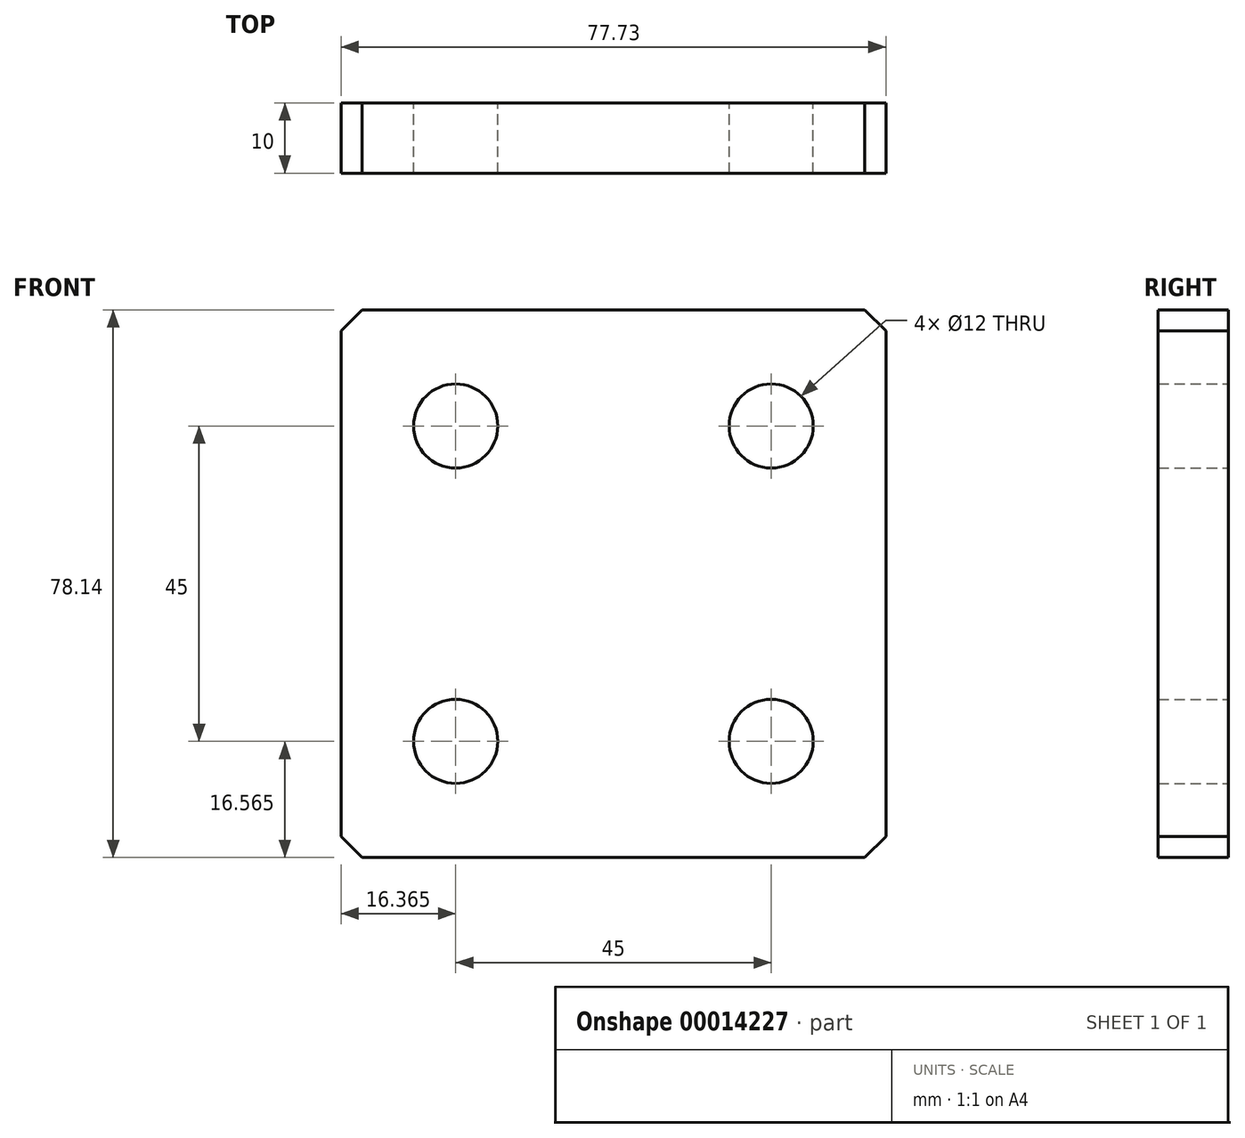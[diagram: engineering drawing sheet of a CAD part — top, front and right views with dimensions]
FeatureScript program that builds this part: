
annotation { "Feature Type Name" : "Feature", "Feature Type Description" : "" }
export const myFeature = defineFeature(function(context is Context, id is Id, definition is map)
    precondition{}
    {
        {
            var Q0;
            Q0=qCreatedBy(makeId("Front.planeOp"),FACE);
            var sketch = newSketch(context, id + "F0", { "sketchPlane" : qUnion([Q0])});
            skPoint(sketch, "E0.rect.middle", {"position": v(-49.6, 29.74) * mm});
            skCircle(sketch, "E1", {"center": v(-27.1, 52.24) * mm, "radius": 6 * mm});
            skCircle(sketch, "E2", {"center": v(-72.1, 52.24) * mm, "radius": 6 * mm});
            skLineSegment(sketch, "E0.rect.right", {"start": v(-72.1, 7.24) * mm, "end": v(-72.1, 52.24) * mm, "construction": true});
            skLineSegment(sketch, "E0.rect.left", {"start": v(-27.1, 7.24) * mm, "end": v(-27.1, 52.24) * mm, "construction": true});
            skLineSegment(sketch, "E0.rect.top", {"start": v(-27.1, 52.24) * mm, "end": v(-72.1, 52.24) * mm, "construction": true});
            skLineSegment(sketch, "E0.rect.bottom", {"start": v(-27.1, 7.24) * mm, "end": v(-72.1, 7.24) * mm, "construction": true});
            skCircle(sketch, "E3", {"center": v(-72.1, 7.24) * mm, "radius": 6 * mm});
            skCircle(sketch, "E4", {"center": v(-27.1, 7.24) * mm, "radius": 6 * mm});
            skLineSegment(sketch, "E5", {"start": v(-49.6, 29.74) * mm, "end": v(-49.6, 67.24) * mm, "construction": true});
            skLineSegment(sketch, "E6", {"start": v(-49.6, 67.24) * mm, "end": v(-49.6, -7.76) * mm, "construction": true});
            skLineSegment(sketch, "E7.rect.bottom", {"start": v(-88.47, 68.8) * mm, "end": v(-10.74, 68.8) * mm});
            skLineSegment(sketch, "E7.rect.top", {"start": v(-88.47, -9.33) * mm, "end": v(-10.74, -9.33) * mm});
            skLineSegment(sketch, "E7.rect.left", {"start": v(-88.47, 68.8) * mm, "end": v(-88.47, -9.33) * mm});
            skLineSegment(sketch, "E7.rect.right", {"start": v(-10.74, 68.8) * mm, "end": v(-10.74, -9.33) * mm});
            skSolve(sketch);
        }
        {
            var Q0;
            Q0=qSketchRegion(id+"F0",true);
            extrude(context, id + "F1", {"entities" : qUnion([Q0]), "endBound" : BoundingType.SYMMETRIC, "depth" : 10 * mm});
        }
        {
            var Q0;
            Q0=makeQuery(id+"F1.opExtrude","SWEPT_EDGE",EDGE,{"disambiguationData":[OSD([sQuery(id+"F0.wireOp",EDGE,"E7.rect.bottom"),sQuery(id+"F0.wireOp",EDGE,"E7.rect.left")])]});
            var Q1;
            Q1=makeQuery(id+"F1.opExtrude","SWEPT_EDGE",EDGE,{"disambiguationData":[OSD([sQuery(id+"F0.wireOp",EDGE,"E7.rect.bottom"),sQuery(id+"F0.wireOp",EDGE,"E7.rect.right")])]});
            var Q2;
            Q2=makeQuery(id+"F1.opExtrude","SWEPT_EDGE",EDGE,{"disambiguationData":[OSD([sQuery(id+"F0.wireOp",EDGE,"E7.rect.top"),sQuery(id+"F0.wireOp",EDGE,"E7.rect.right")])]});
            var Q3;
            Q3=makeQuery(id+"F1.opExtrude","SWEPT_EDGE",EDGE,{"disambiguationData":[OSD([sQuery(id+"F0.wireOp",EDGE,"E7.rect.top"),sQuery(id+"F0.wireOp",EDGE,"E7.rect.left")])]});
            chamfer(context, id + "F2", {"entities" : qUnion([Q0, Q1, Q2, Q3]), "width" : 3 * mm, "tangentPropagation" : true});
        }
    });
